# Revit family: 702-73-103-DN50-300
name_source: partatom
category: Pipe Accessories
units: mm (PartAtom-declared; Revit-internal decimal feet)

## family parameters
Always vertical = Yes
Cut with Voids When Loaded = No
Part Type = Valve - Breaks Into
Round Connector Dimension = Use Diameter
Shared = No
Work Plane-Based = No

## types (9) — shared parameters
DN050_PN10 = 702-0050-10-0000093
DN065_PN10 = 702-0065-10-0000093
DN080_PN10 = 702-0080-10-0000095
DN100_PN10 = 702-0100-10-0000103
DN125_PN10 = 702-0125-10-0000104
DN150_PN10 = 702-0150-10-0000105
DN200_PN10 = 702-0200-10-0000288
DN250_PN10 = 702-0250-10-0000288
DN300_PN10 = 702-0300-10-0000252
Description_ = AVK KNIFE GATE VALVE
Search_table = 702-73-103-DN50-300
URL product pages = https://www.avkvalves.com

## per-type parameters (varying)
- DN 050: B2_Ref=78 mm; Body_width=87 mm; Bonnet_height=516 mm; Bonnet_height_2=284 mm; D=130 mm; Flange_Thickness=5 mm  [stored 0.0164042 ft]; H=568 mm; H1=588 mm; H1_Ref_2=90 mm; H3=634 mm; H4=160 mm; H4_half=120 mm; H4_half_ref=70 mm; HW_Dia=10 mm  [stored 0.0328084 ft]; H_2=284 mm; H_Ref=113 mm; Ho=407 mm; ID=25 mm  [stored 0.082021 ft]; L=43 mm  [stored 0.141076 ft]; L2=47 mm  [stored 0.154199 ft]; Name_Ref=169 mm; Neck_Rod=10 mm  [stored 0.0328084 ft]; Nominal Diameter (DN)=50 mm  [stored 0.164042 ft]; Top_flange=63 mm; Top_flange2=20 mm  [stored 0.0656168 ft]; W2=65 mm  [stored 0.213255 ft]; W3=54 mm; W3_ref=130 mm; W4=36 mm; W5=30 mm  [stored 0.0984252 ft]; W6=20 mm  [stored 0.0656168 ft]
- DN 065: B2_Ref=86 mm; Body_width=95 mm; Bonnet_height=539 mm; Bonnet_height_2=297 mm; D=143 mm; Flange_Thickness=5 mm  [stored 0.0164042 ft]; H=593 mm; H1=613 mm; H1_Ref_2=90 mm; H3=665 mm; H4=160 mm; H4_half=120 mm; H4_half_ref=70 mm; HW_Dia=10 mm  [stored 0.0328084 ft]; H_2=297 mm; H_Ref=124 mm; Ho=444 mm; ID=33 mm; L=46 mm  [stored 0.150919 ft]; L2=51 mm  [stored 0.167323 ft]; Name_Ref=186 mm; Neck_Rod=10 mm  [stored 0.0328084 ft]; Nominal Diameter (DN)=65 mm  [stored 0.213255 ft]; Top_flange=63 mm; Top_flange2=20 mm  [stored 0.0656168 ft]; W2=72 mm; W3=60 mm  [stored 0.19685 ft]; W3_ref=143 mm; W4=40 mm  [stored 0.131234 ft]; W5=33 mm; W6=22 mm
- DN 080: B2_Ref=110 mm; Body_width=122 mm; Bonnet_height=565 mm; Bonnet_height_2=311 mm; D=183 mm; Flange_Thickness=5 mm  [stored 0.0164042 ft]; H=622 mm; H1=645 mm; H1_Ref_2=100 mm; H3=714 mm; H4=160 mm; H4_half=120 mm; H4_half_ref=70 mm; HW_Dia=15 mm  [stored 0.0492126 ft]; H_2=311 mm; H_Ref=159 mm; Ho=499 mm; ID=40 mm  [stored 0.131234 ft]; L=46 mm  [stored 0.150919 ft]; L2=51 mm  [stored 0.167323 ft]; Name_Ref=238 mm; Neck_Rod=10 mm  [stored 0.0328084 ft]; Nominal Diameter (DN)=80 mm; Top_flange=63 mm; Top_flange2=23 mm  [stored 0.0754593 ft]; W2=92 mm; W3=76 mm; W3_ref=183 mm; W4=51 mm  [stored 0.167323 ft]; W5=42 mm; W6=28 mm
- DN 100: B2_Ref=121 mm; Body_width=135 mm; Bonnet_height=596 mm; Bonnet_height_2=328 mm; D=202 mm; Flange_Thickness=5 mm  [stored 0.0164042 ft]; H=656 mm; H1=680 mm; H1_Ref_2=110 mm; H3=757 mm; H4=160 mm; H4_half=120 mm; H4_half_ref=70 mm; HW_Dia=15 mm  [stored 0.0492126 ft]; H_2=328 mm; H_Ref=175 mm; Ho=582 mm; ID=50 mm  [stored 0.164042 ft]; L=52 mm  [stored 0.170604 ft]; L2=57 mm; Name_Ref=263 mm; Neck_Rod=10 mm  [stored 0.0328084 ft]; Nominal Diameter (DN)=100 mm; Top_flange=63 mm; Top_flange2=24 mm  [stored 0.0787402 ft]; W2=101 mm; W3=84 mm; W3_ref=202 mm; W4=56 mm  [stored 0.183727 ft]; W5=47 mm  [stored 0.154199 ft]; W6=31 mm
- DN 125: B2_Ref=137 mm; Body_width=153 mm; Bonnet_height=632 mm; Bonnet_height_2=348 mm; D=229 mm; Flange_Thickness=5 mm  [stored 0.0164042 ft]; H=695 mm; H1=716 mm; H1_Ref_2=148 mm; H3=810 mm; H4=160 mm; H4_half=120 mm; H4_half_ref=70 mm; HW_Dia=25 mm  [stored 0.082021 ft]; H_2=348 mm; H_Ref=198 mm; Ho=618 mm; ID=63 mm; L=56 mm  [stored 0.183727 ft]; L2=62 mm; Name_Ref=298 mm; Neck_Rod=10 mm  [stored 0.0328084 ft]; Nominal Diameter (DN)=125 mm; Top_flange=63 mm; Top_flange2=21 mm  [stored 0.0688976 ft]; W2=115 mm; W3=95 mm; W3_ref=229 mm; W4=64 mm; W5=53 mm; W6=35 mm
- DN 150: B2_Ref=160 mm; Body_width=178 mm; Bonnet_height=789 mm; Bonnet_height_2=434 mm; D=267 mm; Flange_Thickness=5 mm  [stored 0.0164042 ft]; H=868 mm; H1=798 mm; H1_Ref_2=148 mm; H3=1003 mm; H4=160 mm; H4_half=120 mm; H4_half_ref=70 mm; HW_Dia=25 mm  [stored 0.082021 ft]; H_2=434 mm; H_Ref=231 mm; Ho=732 mm; ID=75 mm; L=56 mm  [stored 0.183727 ft]; L2=62 mm; Name_Ref=347 mm; Neck_Rod=10 mm  [stored 0.0328084 ft]; Nominal Diameter (DN)=150 mm; Top_flange=63 mm; Top_flange2=-70 mm  [stored -0.229659 ft]; W2=134 mm; W3=111 mm; W3_ref=267 mm; W4=74 mm; W5=62 mm; W6=41 mm
- DN 200: B2_Ref=196 mm; Body_width=217 mm; Bonnet_height=881 mm; Bonnet_height_2=485 mm; D=326 mm; Flange_Thickness=10 mm  [stored 0.0328084 ft]; H=969 mm; H1=898 mm; H1_Ref_2=158 mm; H3=1134 mm; H4=200 mm; H4_half=160 mm; H4_half_ref=90 mm; HW_Dia=25 mm  [stored 0.082021 ft]; H_2=485 mm; H_Ref=283 mm; Ho=882 mm; ID=100 mm; L=60 mm  [stored 0.19685 ft]; L2=66 mm  [stored 0.216535 ft]; Name_Ref=424 mm; Neck_Rod=20 mm  [stored 0.0656168 ft]; Nominal Diameter (DN)=200 mm; Top_flange=63 mm; Top_flange2=-71 mm  [stored -0.23294 ft]; W2=163 mm; W3=136 mm; W3_ref=326 mm; W4=91 mm; W5=75 mm; W6=50 mm  [stored 0.164042 ft]
- DN 250: B2_Ref=237 mm; Body_width=263 mm; Bonnet_height=1122 mm; Bonnet_height_2=617 mm; D=395 mm; Flange_Thickness=10 mm  [stored 0.0328084 ft]; H=1234 mm; H1=1006 mm; H1_Ref_2=165 mm; H3=1433 mm; H4=315 mm; H4_half=275 mm; H4_half_ref=148 mm; HW_Dia=30 mm  [stored 0.0984252 ft]; H_2=617 mm; H_Ref=342 mm; Ho=1044 mm; ID=125 mm; L=68 mm  [stored 0.223097 ft]; L2=75 mm; Name_Ref=514 mm; Neck_Rod=20 mm  [stored 0.0656168 ft]; Nominal Diameter (DN)=250 mm; Top_flange=88 mm; Top_flange2=-228 mm  [stored -0.748031 ft]; W2=198 mm; W3=165 mm; W3_ref=395 mm; W4=110 mm; W5=91 mm; W6=61 mm
- DN 300: B2_Ref=271 mm; Body_width=301 mm; Bonnet_height=1226 mm; Bonnet_height_2=675 mm; D=451 mm; Flange_Thickness=15 mm  [stored 0.0492126 ft]; H=1349 mm; H1=1124 mm; H1_Ref_2=190 mm; H3=1575 mm; H4=315 mm; H4_half=275 mm; H4_half_ref=148 mm; HW_Dia=30 mm  [stored 0.0984252 ft]; H_2=675 mm; H_Ref=391 mm; Ho=1219 mm; ID=150 mm; L=78 mm; L2=86 mm; Name_Ref=586 mm; Neck_Rod=30 mm  [stored 0.0984252 ft]; Nominal Diameter (DN)=300 mm; Top_flange=88 mm; Top_flange2=-225 mm  [stored -0.738189 ft]; W2=226 mm; W3=188 mm; W3_ref=451 mm; W4=125 mm; W5=104 mm; W6=70 mm

note: [stored X ft] marks values corroborated as IEEE doubles in the binary element streams (Revit-internal decimal feet)

## geometry (parser evidence)
native form markers: Sweep x6
no freeform markers — native parametric forms only
